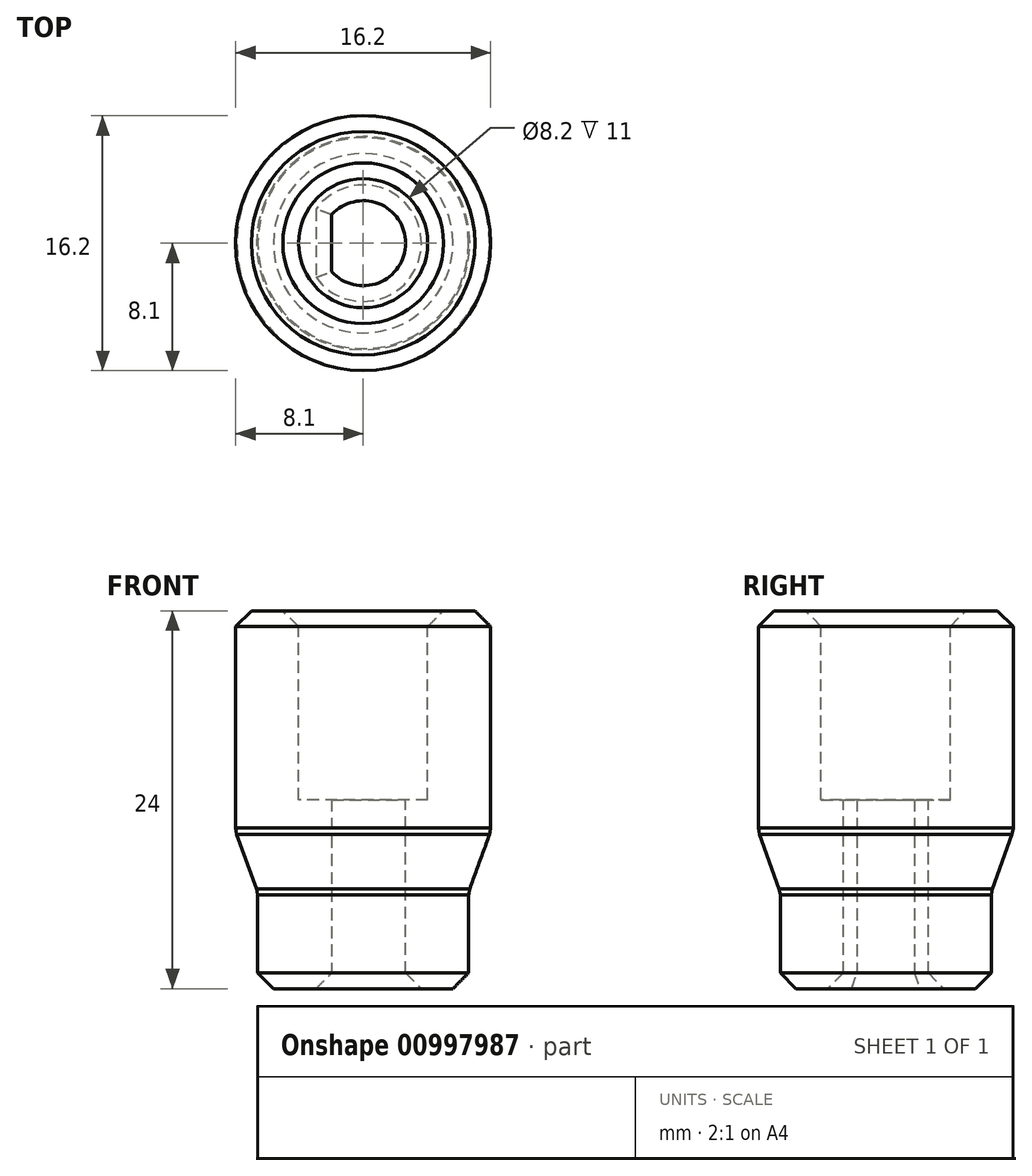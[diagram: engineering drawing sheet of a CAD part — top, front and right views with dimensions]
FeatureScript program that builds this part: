
annotation { "Feature Type Name" : "Feature", "Feature Type Description" : "" }
export const myFeature = defineFeature(function(context is Context, id is Id, definition is map)
    precondition{}
    {
        {
            var Q0;
            Q0=qCreatedBy(makeId("Front.planeOp"),FACE);
            var sketch = newSketch(context, id + "F0", { "sketchPlane" : qUnion([Q0])});
            skLineSegment(sketch, "E0", {"start": v(-2.7, 0) * mm, "end": v(-2.7, 12) * mm});
            skLineSegment(sketch, "E1", {"start": v(-2.7, 12) * mm, "end": v(-4.1, 12) * mm});
            skLineSegment(sketch, "E2", {"start": v(-4.1, 12) * mm, "end": v(-4.1, 24) * mm});
            skLineSegment(sketch, "E3", {"start": v(-4.1, 24) * mm, "end": v(-8.1, 24) * mm});
            skLineSegment(sketch, "E4", {"start": v(-8.1, 24) * mm, "end": v(-8.1, 10) * mm});
            skLineSegment(sketch, "E5", {"start": v(-2.7, 0) * mm, "end": v(-6.7, 0) * mm});
            skLineSegment(sketch, "E6", {"start": v(-6.7, 0) * mm, "end": v(-6.7, 6.15) * mm});
            skLineSegment(sketch, "E7", {"start": v(-6.7, 6.15) * mm, "end": v(-8.1, 10) * mm});
            skLineSegment(sketch, "E8", {"start": v(0, 17.81) * mm, "end": v(0, 2.78) * mm, "construction": true});
            skSolve(sketch);
        }
        {
            var Q0;
            Q0=makeQuery(id+"F0.imprint","IMPRINT",FACE,{"disambiguationData":[TD([[makeQuery(id+"F0.imprint","IMPRINT",EDGE,{"derivedFrom":sQuery(id+"F0.wireOp",EDGE,"E0")}),1.0]])]});
            var Q1;
            Q1=sQuery(id+"F0.wireOp",EDGE,"E8");
            revolve(context, id + "F1", {"surfaceOperationType" : NewSurfaceOperationType.NEW, "entities" : qUnion([Q0]), "axis" : qUnion([Q1]), "revolveType" : RevolveType.FULL});
        }
        {
            var Q0;
            Q0=qCreatedBy(makeId("Top.planeOp"),FACE);
            var sketch = newSketch(context, id + "F2", { "sketchPlane" : qUnion([Q0])});
            skCircle(sketch, "E9.0", {"center": v(0, 0) * mm, "radius": 2.7 * mm});
            skLineSegment(sketch, "E10", {"start": v(-2, -1.81) * mm, "end": v(-2, 1.81) * mm});
            skSolve(sketch);
        }
        {
            var Q0;
            {var subQ0=sQuery(id+"F2.wireOp",EDGE,"E10");Q0=makeQuery(id+"F2.imprint","IMPRINT",FACE,{"disambiguationData":[TD([[makeQuery(id+"F2.imprint","IMPRINT",EDGE,{"derivedFrom":subQ0}),1.0]])]});}
            extrude(context, id + "F3", {"entities" : qUnion([Q0]), "operationType" : NewBodyOperationType.ADD, "depth" : 12 * mm, "offsetDistance" : 25 * mm});
        }
        {
            var Q0;
            Q0=makeQuery(id+"F1.opRevolve","SWEPT_EDGE",EDGE,{"disambiguationData":[OSD([sQuery(id+"F0.wireOp",EDGE,"E3"),sQuery(id+"F0.wireOp",EDGE,"E4")])]});
            var Q1;
            Q1=makeQuery(id+"F1.opRevolve","SWEPT_EDGE",EDGE,{"disambiguationData":[OSD([sQuery(id+"F0.wireOp",EDGE,"E5"),sQuery(id+"F0.wireOp",EDGE,"E6")])]});
            var Q2;
            Q2=makeQuery(id+"F1.opRevolve","SWEPT_EDGE",EDGE,{"disambiguationData":[OSD([sQuery(id+"F0.wireOp",EDGE,"E0"),sQuery(id+"F0.wireOp",EDGE,"E5")])]});
            var Q3;
            Q3=makeQuery(id+"F3.opExtrude","CAP_EDGE",EDGE,{"disambiguationData":[OSD([sQuery(id+"F2.wireOp",EDGE,"E10")])],"isStart":true});
            var Q4;
            Q4=makeQuery(id+"F1.opRevolve","SWEPT_EDGE",EDGE,{"disambiguationData":[OSD([sQuery(id+"F0.wireOp",EDGE,"E2"),sQuery(id+"F0.wireOp",EDGE,"E3")])]});
            chamfer(context, id + "F4", {"entities" : qUnion([Q0, Q1, Q2, Q3, Q4]), "width" : 1 * mm, "tangentPropagation" : true});
        }
        {
            var Q0;
            Q0=makeQuery(id+"F1.opRevolve","SWEPT_EDGE",EDGE,{"disambiguationData":[OSD([sQuery(id+"F0.wireOp",EDGE,"E4"),sQuery(id+"F0.wireOp",EDGE,"E7")])]});
            var Q1;
            Q1=makeQuery(id+"F1.opRevolve","SWEPT_EDGE",EDGE,{"disambiguationData":[OSD([sQuery(id+"F0.wireOp",EDGE,"E6"),sQuery(id+"F0.wireOp",EDGE,"E7")])]});
            chamfer(context, id + "F5", {"entities" : qUnion([Q0, Q1]), "width" : 1.2 * mm, "tangentPropagation" : true});
        }
    });
